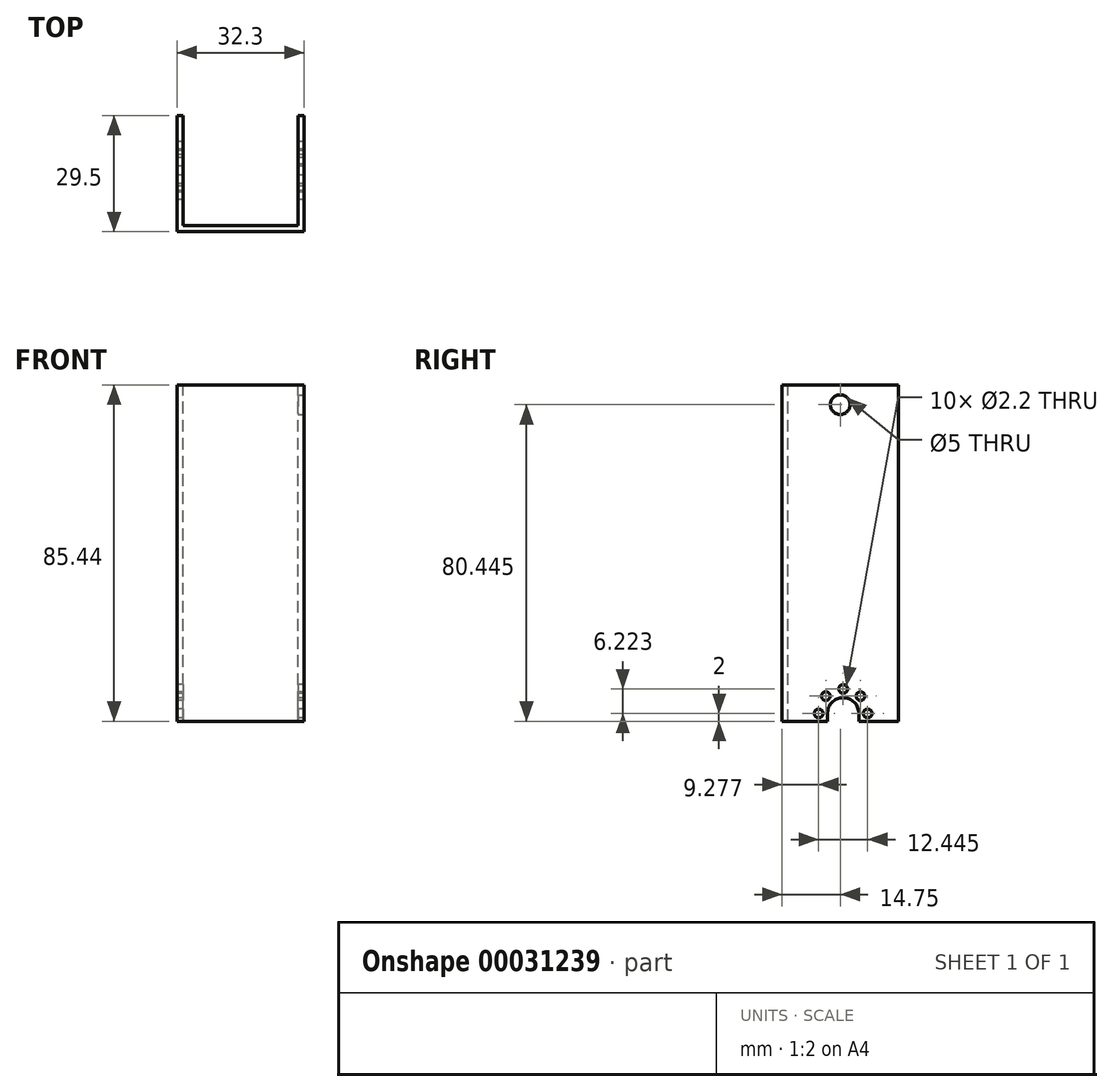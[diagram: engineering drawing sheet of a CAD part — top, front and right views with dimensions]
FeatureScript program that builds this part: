
annotation { "Feature Type Name" : "Feature", "Feature Type Description" : "" }
export const myFeature = defineFeature(function(context is Context, id is Id, definition is map)
    precondition{}
    {
        {
            var Q0;
            Q0=qCreatedBy(makeId("Front.planeOp"),FACE);
            var sketch = newSketch(context, id + "F0", { "sketchPlane" : qUnion([Q0])});
            skLineSegment(sketch, "E0.bottom", {"start": v(0, 0) * mm, "end": v(1.5, 0) * mm});
            skLineSegment(sketch, "E0.top", {"start": v(0, 86.95) * mm, "end": v(32.3, 86.95) * mm});
            skLineSegment(sketch, "E0.left", {"start": v(0, 0) * mm, "end": v(0, 86.95) * mm});
            skLineSegment(sketch, "E0.right", {"start": v(32.3, 0) * mm, "end": v(32.3, 86.95) * mm});
            skLineSegment(sketch, "E1.top", {"start": v(1.5, 85.45) * mm, "end": v(30.8, 85.45) * mm});
            skLineSegment(sketch, "E1.left", {"start": v(1.5, 0) * mm, "end": v(1.5, 85.45) * mm});
            skLineSegment(sketch, "E1.right", {"start": v(30.8, 0) * mm, "end": v(30.8, 85.45) * mm});
            skLineSegment(sketch, "E2.trimOffspring", {"start": v(30.8, 0) * mm, "end": v(32.3, 0) * mm});
            skSolve(sketch);
        }
        {
            var Q0;
            Q0=qSketchRegion(id+"F0",true);
            extrude(context, id + "F1", {"entities" : qUnion([Q0]), "depth" : 28 * mm});
        }
        {
            var Q0;
            Q0=makeQuery(id+"F1.opExtrude","SWEPT_FACE",FACE,{"disambiguationData":[OSD([sQuery(id+"F0.wireOp",EDGE,"E0.left")])]});
            var sketch = newSketch(context, id + "F2", { "sketchPlane" : qUnion([Q0])});
            skArc(sketch, "E3", {"start": v(18, 2) * mm, "mid": v(14, 6) * mm, "end": v(10, 2) * mm});
            skCircle(sketch, "E4", {"center": v(20.22, 2) * mm, "radius": 1.1 * mm});
            skCircle(sketch, "E5.1.0", {"center": v(18.4, 6.4) * mm, "radius": 1.1 * mm});
            skCircle(sketch, "E5.2.0", {"center": v(14, 8.22) * mm, "radius": 1.1 * mm});
            skCircle(sketch, "E5.3.0", {"center": v(9.6, 6.4) * mm, "radius": 1.1 * mm});
            skCircle(sketch, "E5.4.0", {"center": v(7.78, 2) * mm, "radius": 1.1 * mm});
            skLineSegment(sketch, "E6", {"start": v(10, 2) * mm, "end": v(10, 0) * mm});
            skLineSegment(sketch, "E7", {"start": v(18, 2) * mm, "end": v(18, 0) * mm});
            skLineSegment(sketch, "E8", {"start": v(10, 0) * mm, "end": v(18, 0) * mm});
            skLineSegment(sketch, "E9", {"start": v(14, 86.95) * mm, "end": v(14, 0) * mm, "construction": true});
            skPoint(sketch, "E10", {"position": v(14, 0) * mm});
            skLineSegment(sketch, "E11", {"start": v(2.78, 0) * mm, "end": v(0, 0) * mm});
            skLineSegment(sketch, "E12", {"start": v(0, 0) * mm, "end": v(0, 85.45) * mm});
            skLineSegment(sketch, "E13.MirrorCS", {"start": v(28, 0) * mm, "end": v(28, 85.45) * mm});
            skLineSegment(sketch, "E14.MirrorCS", {"start": v(25.22, 0) * mm, "end": v(28, 0) * mm});
            skPoint(sketch, "E15.MirrorCS.end.orphan", {"position": v(28, 85.45) * mm});
            skPoint(sketch, "E15.MirrorCS.start.orphan", {"position": v(25.22, 0) * mm});
            skSolve(sketch);
        }
        {
            var Q0;
            Q0=qSketchRegion(id+"F2",true);
            extrude(context, id + "F3", {"entities" : qUnion([Q0]), "operationType" : NewBodyOperationType.REMOVE, "endBound" : BoundingType.THROUGH_ALL, "oppositeDirection" : true, "depth" : 25 * mm});
        }
        {
            var Q0;
            Q0=makeQuery(id+"F1.opExtrude","SWEPT_FACE",FACE,{"disambiguationData":[OSD([sQuery(id+"F0.wireOp",EDGE,"E0.top")])]});
            var sketch = newSketch(context, id + "F4", { "sketchPlane" : qUnion([Q0])});
            skLineSegment(sketch, "E16", {"start": v(16.15, 0) * mm, "end": v(16.15, -28) * mm, "construction": true});
            skLineSegment(sketch, "E17", {"start": v(0, -14) * mm, "end": v(32.3, -14) * mm, "construction": true});
            skCircle(sketch, "E18", {"center": v(6.15, -4) * mm, "radius": 1.1 * mm});
            skCircle(sketch, "E19.MirrorC", {"center": v(26.15, -4) * mm, "radius": 1.1 * mm});
            skCircle(sketch, "E20.MirrorC", {"center": v(6.15, -24) * mm, "radius": 1.1 * mm});
            skCircle(sketch, "E21.MirrorC", {"center": v(26.15, -24) * mm, "radius": 1.1 * mm});
            skSolve(sketch);
        }
        {
            var Q0;
            Q0=qSketchRegion(id+"F4",true);
            extrude(context, id + "F5", {"entities" : qUnion([Q0]), "operationType" : NewBodyOperationType.REMOVE, "endBound" : BoundingType.UP_TO_NEXT, "oppositeDirection" : true, "depth" : 25 * mm});
        }
        {
            var Q0;
            Q0=makeQuery(id+"F1.opExtrude","SWEPT_FACE",FACE,{"disambiguationData":[OSD([sQuery(id+"F0.wireOp",EDGE,"E0.right")])]});
            var sketch = newSketch(context, id + "F6", { "sketchPlane" : qUnion([Q0])});
            skLineSegment(sketch, "E22.bottom", {"start": v(-28, 86.95) * mm, "end": v(-29.5, 86.95) * mm});
            skLineSegment(sketch, "E22.top", {"start": v(-28, 0) * mm, "end": v(-29.5, 0) * mm});
            skLineSegment(sketch, "E22.left", {"start": v(-28, 86.95) * mm, "end": v(-28, 0) * mm});
            skLineSegment(sketch, "E22.right", {"start": v(-29.5, 86.95) * mm, "end": v(-29.5, 0) * mm});
            skLineSegment(sketch, "E23", {"start": v(-14, 86.95) * mm, "end": v(-14, 0) * mm, "construction": true});
            skLineSegment(sketch, "E24.MirrorCS", {"start": v(0, 86.95) * mm, "end": v(0, 0) * mm});
            skLineSegment(sketch, "E25.MirrorCS", {"start": v(1.5, 86.95) * mm, "end": v(1.5, 0) * mm});
            skLineSegment(sketch, "E26.MirrorCS", {"start": v(0, 86.95) * mm, "end": v(1.5, 86.95) * mm});
            skLineSegment(sketch, "E27.MirrorCS", {"start": v(0, 0) * mm, "end": v(1.5, 0) * mm});
            skSolve(sketch);
        }
        {
            var Q0;
            Q0=makeQuery(id+"F6.imprint","IMPRINT",FACE,{"disambiguationData":[TD([[makeQuery(id+"F6.imprint","IMPRINT",EDGE,{"derivedFrom":sQuery(id+"F6.wireOp",EDGE,"E22.bottom")}),1.0]])]});
            extrude(context, id + "F7", {"entities" : qUnion([Q0]), "operationType" : NewBodyOperationType.ADD, "oppositeDirection" : true, "depth" : 32.3 * mm});
        }
        {
            var Q0;
            Q0=makeQuery(id+"F7.opExtrude","SWEPT_FACE",FACE,{"disambiguationData":[OSD([sQuery(id+"F6.wireOp",EDGE,"E22.right")])]});
            var sketch = newSketch(context, id + "F8", { "sketchPlane" : qUnion([Q0])});
            skPoint(sketch, "E28.centerSnap0", {"position": v(16.15, 0) * mm});
            skLineSegment(sketch, "E29.bottom", {"start": v(0, 86.95) * mm, "end": v(32.3, 86.95) * mm});
            skLineSegment(sketch, "E29.top", {"start": v(0, 85.45) * mm, "end": v(32.3, 85.45) * mm});
            skLineSegment(sketch, "E29.left", {"start": v(0, 86.95) * mm, "end": v(0, 85.45) * mm});
            skLineSegment(sketch, "E29.right", {"start": v(32.3, 86.95) * mm, "end": v(32.3, 85.45) * mm});
            skPoint(sketch, "E29.middle", {"position": v(16.15, 86.2) * mm});
            skLineSegment(sketch, "E30.bottom", {"start": v(1.5, 85.45) * mm, "end": v(30.8, 85.45) * mm});
            skLineSegment(sketch, "E30.top", {"start": v(1.5, 55.45) * mm, "end": v(30.8, 55.45) * mm});
            skLineSegment(sketch, "E30.left", {"start": v(1.5, 85.45) * mm, "end": v(1.5, 55.45) * mm});
            skLineSegment(sketch, "E30.right", {"start": v(30.8, 85.45) * mm, "end": v(30.8, 55.45) * mm});
            skPoint(sketch, "E31", {"position": v(16.15, 85.45) * mm});
            skLineSegment(sketch, "E32.bottom", {"start": v(0, 85.45) * mm, "end": v(1.5, 85.45) * mm});
            skLineSegment(sketch, "E32.top", {"start": v(0, 55.45) * mm, "end": v(1.5, 55.45) * mm});
            skLineSegment(sketch, "E32.left", {"start": v(0, 85.45) * mm, "end": v(0, 55.45) * mm});
            skLineSegment(sketch, "E33.bottom", {"start": v(30.8, 85.45) * mm, "end": v(32.3, 85.45) * mm});
            skLineSegment(sketch, "E33.top", {"start": v(30.8, 55.45) * mm, "end": v(32.3, 55.45) * mm});
            skLineSegment(sketch, "E33.right", {"start": v(32.3, 85.45) * mm, "end": v(32.3, 55.45) * mm});
            skSolve(sketch);
        }
        {
            var Q0;
            Q0=makeQuery(id+"F8.imprint","IMPRINT",FACE,{"disambiguationData":[TD([[makeQuery(id+"F8.imprint","IMPRINT",EDGE,{"derivedFrom":sQuery(id+"F8.wireOp",EDGE,"E30.bottom")}),-1.0]])]});
            var Q1;
            Q1=makeQuery(id+"F8.imprint","IMPRINT",FACE,{"disambiguationData":[TD([[makeQuery(id+"F8.imprint","IMPRINT",EDGE,{"derivedFrom":sQuery(id+"F8.wireOp",EDGE,"E32.bottom")}),-1.0]])]});
            var Q2;
            Q2=makeQuery(id+"F8.imprint","IMPRINT",FACE,{"disambiguationData":[TD([[makeQuery(id+"F8.imprint","IMPRINT",EDGE,{"derivedFrom":sQuery(id+"F8.wireOp",EDGE,"E29.bottom")}),-1.0]])]});
            extrude(context, id + "F9", {"entities" : qUnion([Q0, Q1, Q2]), "operationType" : NewBodyOperationType.REMOVE, "endBound" : BoundingType.THROUGH_ALL, "oppositeDirection" : true, "depth" : 25 * mm});
        }
        {
            var Q0;
            Q0=makeQuery(id+"F7.boolean.opBoolean","MERGE",FACE,{"derivedFrom":[makeQuery(id+"F1.opExtrude","SWEPT_FACE",FACE,{"disambiguationData":[OSD([sQuery(id+"F0.wireOp",EDGE,"E0.right")])]}),makeQuery(id+"F7.opExtrude","CAP_FACE",FACE,{"disambiguationData":[OSD([sQuery(id+"F6.wireOp",EDGE,"E22.bottom"),sQuery(id+"F6.wireOp",EDGE,"E22.top"),sQuery(id+"F6.wireOp",EDGE,"E22.left"),sQuery(id+"F6.wireOp",EDGE,"E22.right")])],"isStart":true})]});
            var sketch = newSketch(context, id + "F10", { "sketchPlane" : qUnion([Q0])});
            skCircle(sketch, "E34", {"center": v(-14.75, 80.45) * mm, "radius": 2.5 * mm});
            skPoint(sketch, "E34.centerSnap0", {"position": v(-14.75, 85.45) * mm});
            skSolve(sketch);
        }
        {
            var Q0;
            Q0 = qSketchRegion(id + "F10", true);
            extrude(context, id + "F11", {"entities" : qUnion([Q0]), "operationType" : NewBodyOperationType.REMOVE, "endBound" : BoundingType.UP_TO_NEXT, "oppositeDirection" : true, "depth" : 25 * mm});
        }
    });
